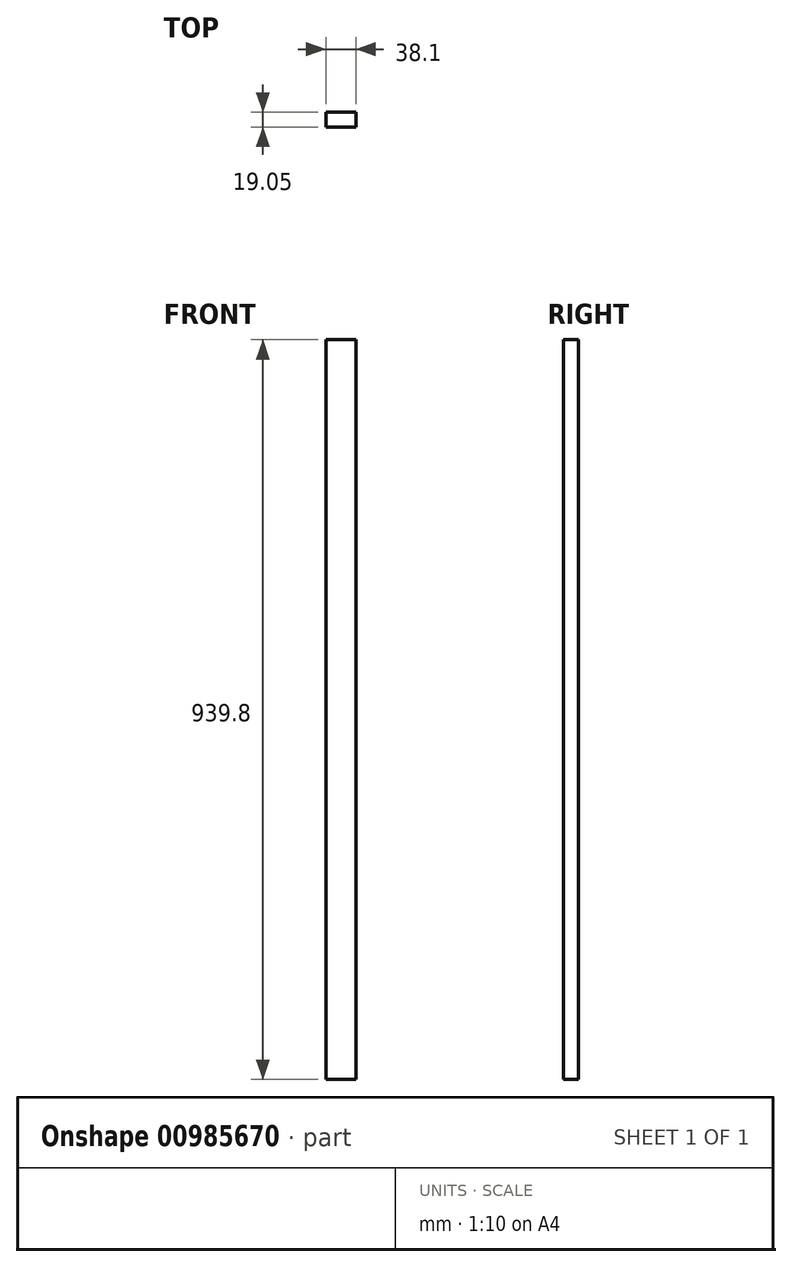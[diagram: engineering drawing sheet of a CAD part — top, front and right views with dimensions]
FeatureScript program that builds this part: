
annotation { "Feature Type Name" : "Feature", "Feature Type Description" : "" }
export const myFeature = defineFeature(function(context is Context, id is Id, definition is map)
    precondition{}
    {
        {
            var Q0;
            Q0=qCreatedBy(makeId("Front.planeOp"),FACE);
            var sketch = newSketch(context, id + "F0", { "sketchPlane" : qUnion([Q0])});
            skLineSegment(sketch, "E0.bottom", {"start": v(19.05, 469.9) * mm, "end": v(-19.05, 469.9) * mm});
            skLineSegment(sketch, "E0.top", {"start": v(19.05, -469.9) * mm, "end": v(-19.05, -469.9) * mm});
            skLineSegment(sketch, "E0.left", {"start": v(19.05, 469.9) * mm, "end": v(19.05, -469.9) * mm});
            skLineSegment(sketch, "E0.right", {"start": v(-19.05, 469.9) * mm, "end": v(-19.05, -469.9) * mm});
            skPoint(sketch, "E0.middle", {"position": v(0, 0) * mm});
            skSolve(sketch);
        }
        {
            var Q0;
            Q0 = qSketchRegion(id + "F0", true);
            extrude(context, id + "F1", {"entities" : qUnion([Q0]), "depth" : 19.05 * mm, "offsetDistance" : 25.4 * mm});
        }
    });
